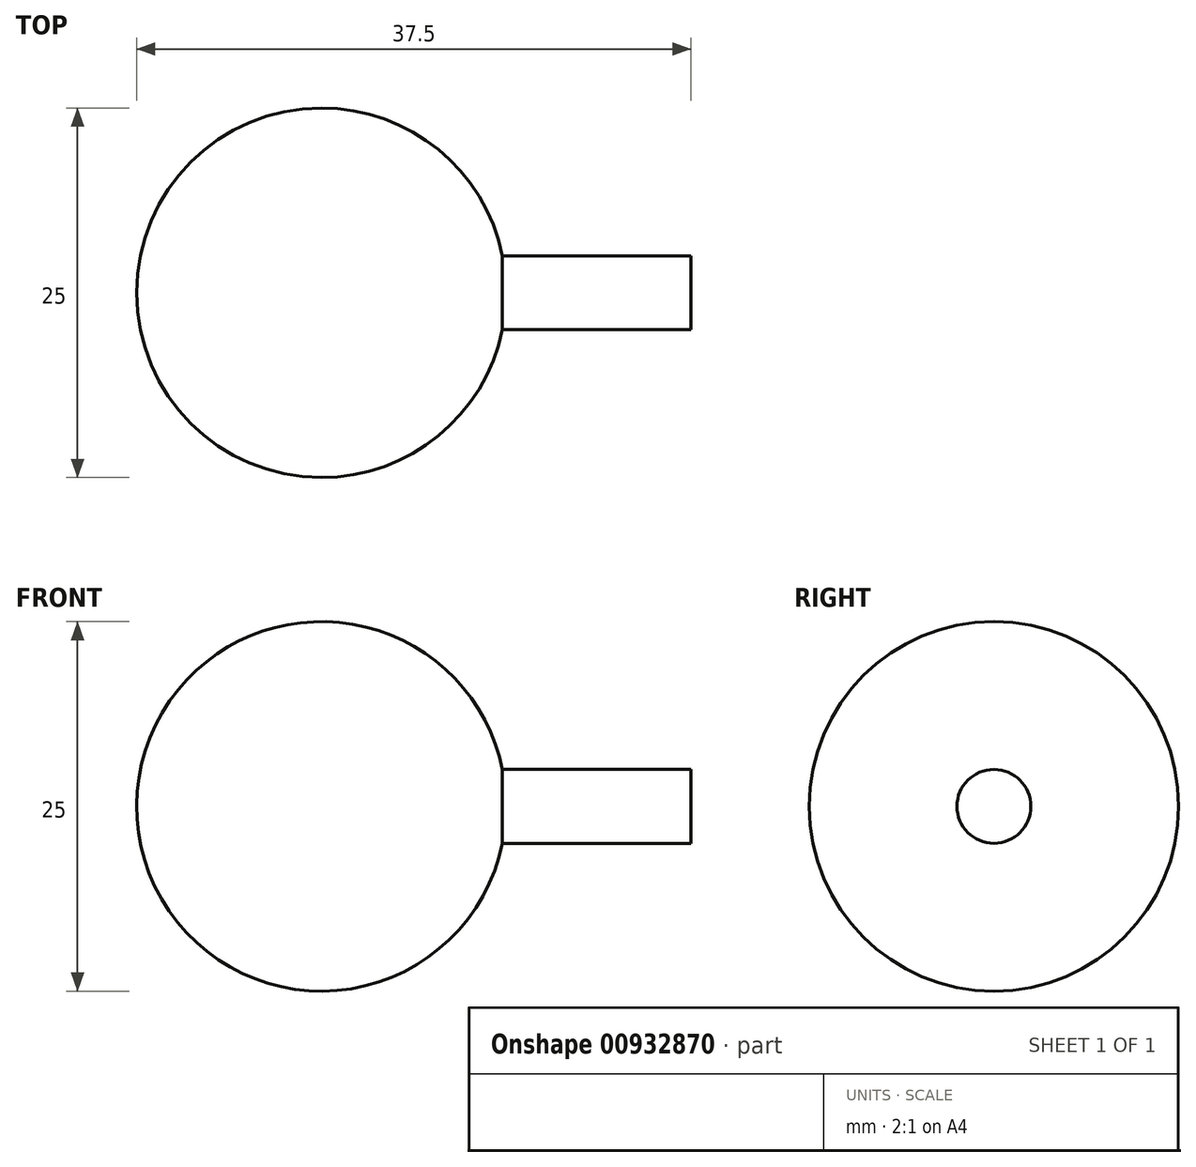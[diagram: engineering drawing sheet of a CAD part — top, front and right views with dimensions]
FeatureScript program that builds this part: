
annotation { "Feature Type Name" : "Feature", "Feature Type Description" : "" }
export const myFeature = defineFeature(function(context is Context, id is Id, definition is map)
    precondition{}
    {
        {
            var Q0;
            Q0=qCreatedBy(makeId("Front.planeOp"),FACE);
            var sketch = newSketch(context, id + "F0", { "sketchPlane" : qUnion([Q0])});
            skCircle(sketch, "E0", {"center": v(0, 0) * mm, "radius": 12.5 * mm});
            skSolve(sketch);
        }
        {
            var Q0;
            Q0=makeQuery(id+"F0.imprint","IMPRINT",FACE,{"disambiguationData":[TD([[makeQuery(id+"F0.imprint","IMPRINT",EDGE,{"derivedFrom":sQuery(id+"F0.wireOp",EDGE,"E0")}),1.0]])]});
            extrude(context, id + "F1", {"entities" : qUnion([Q0]), "endBound" : BoundingType.SYMMETRIC, "depth" : 25 * mm, "offsetDistance" : 25 * mm});
        }
        {
            var Q0;
            Q0=makeQuery(id+"F1.opExtrude","CAP_EDGE",EDGE,{"disambiguationData":[OSD([sQuery(id+"F0.wireOp",EDGE,"E0")])],"isStart":false});
            var Q1;
            Q1=makeQuery(id+"F1.opExtrude","CAP_EDGE",EDGE,{"disambiguationData":[OSD([sQuery(id+"F0.wireOp",EDGE,"E0")])],"isStart":true});
            fillet(context, id + "F2", {"entities" : qUnion([Q0, Q1]), "radius" : 12.5 * mm, "tangentPropagation" : true, "allowEdgeOverflow" : false});
        }
        {
            var Q0;
            Q0=qCreatedBy(makeId("Right.planeOp"),FACE);
            var sketch = newSketch(context, id + "F3", { "sketchPlane" : qUnion([Q0])});
            skCircle(sketch, "E1", {"center": v(0, 0) * mm, "radius": 2.5 * mm});
            skSolve(sketch);
        }
        {
            var Q0;
            Q0 = qSketchRegion(id + "F3", true);
            extrude(context, id + "F4", {"entities" : qUnion([Q0]), "operationType" : NewBodyOperationType.ADD, "depth" : 25 * mm, "offsetDistance" : 25 * mm});
        }
    });
